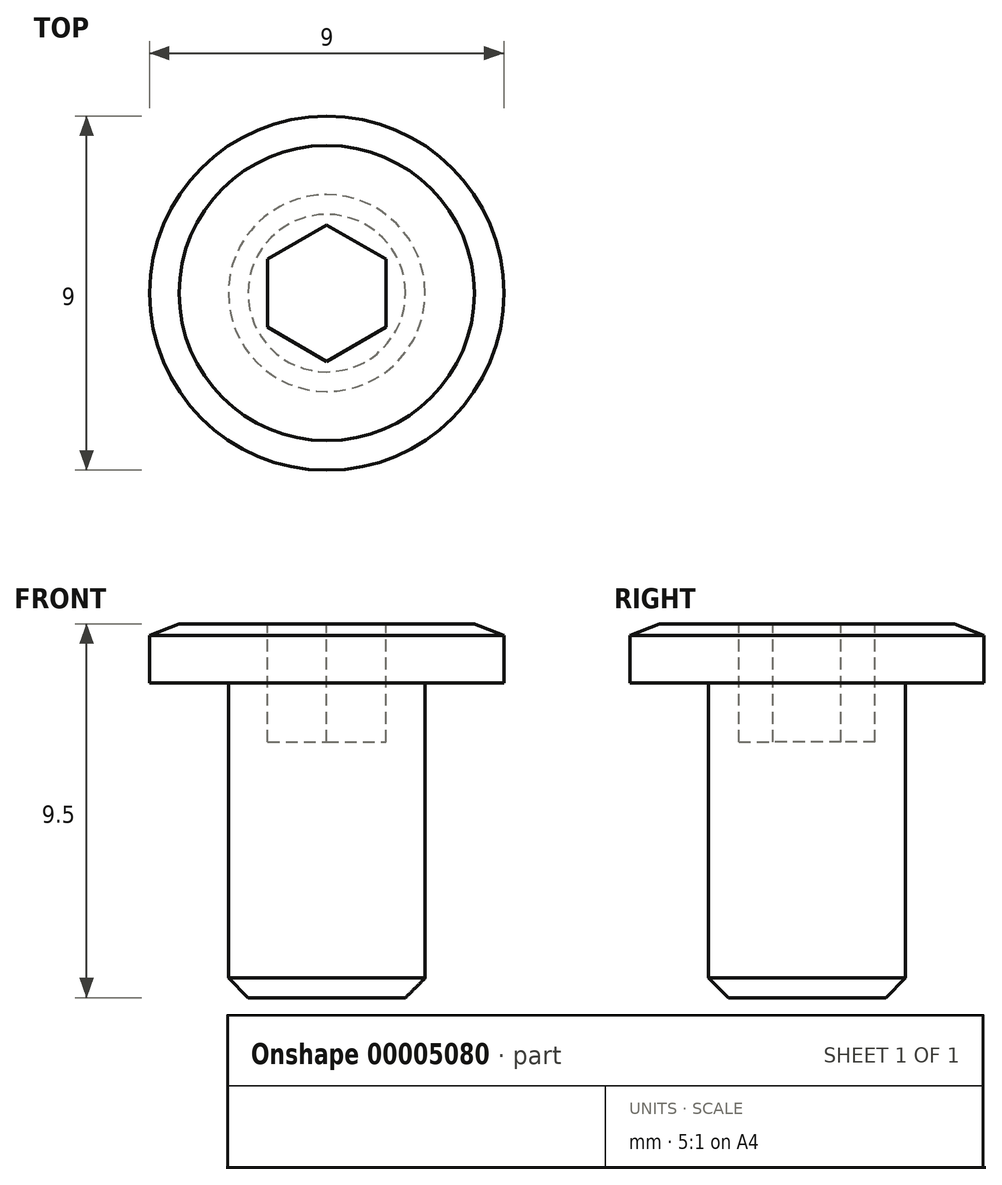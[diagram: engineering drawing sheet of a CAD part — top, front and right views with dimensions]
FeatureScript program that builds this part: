
annotation { "Feature Type Name" : "Feature", "Feature Type Description" : "" }
export const myFeature = defineFeature(function(context is Context, id is Id, definition is map)
    precondition{}
    {
        {
            var Q0;
            Q0=qCreatedBy(makeId("Front.planeOp"),FACE);
            var sketch = newSketch(context, id + "F0", { "sketchPlane" : qUnion([Q0])});
            skLineSegment(sketch, "E0", {"start": v(0, 0) * mm, "end": v(2.5, 0) * mm});
            skLineSegment(sketch, "E1", {"start": v(2.5, 0) * mm, "end": v(2.5, 8) * mm});
            skLineSegment(sketch, "E2", {"start": v(2.5, 8) * mm, "end": v(4.5, 8) * mm});
            skLineSegment(sketch, "E3", {"start": v(4.5, 8) * mm, "end": v(4.5, 9.2) * mm});
            skLineSegment(sketch, "E4", {"start": v(0, 9.5) * mm, "end": v(0, 0) * mm});
            skLineSegment(sketch, "E5", {"start": v(0, 9.5) * mm, "end": v(3.75, 9.5) * mm});
            skLineSegment(sketch, "E6", {"start": v(3.75, 9.5) * mm, "end": v(4.5, 9.2) * mm});
            skSolve(sketch);
        }
        {
            var Q0;
            Q0=makeQuery(id+"F0.imprint","IMPRINT",FACE,{"disambiguationData":[TD([[makeQuery(id+"F0.imprint","IMPRINT",EDGE,{"derivedFrom":sQuery(id+"F0.wireOp",EDGE,"E0")}),1.0]])]});
            var Q1;
            Q1=sQuery(id+"F0.wireOp",EDGE,"E4");
            revolve(context, id + "F1", {"entities" : qUnion([Q0]), "axis" : qUnion([Q1]), "revolveType" : RevolveType.FULL});
        }
        {
            var Q0;
            Q0=makeQuery(id+"F1.opRevolve","SWEPT_EDGE",EDGE,{"disambiguationData":[OSD([sQuery(id+"F0.wireOp",EDGE,"E0"),sQuery(id+"F0.wireOp",EDGE,"E1")])]});
            chamfer(context, id + "F2", {"entities" : qUnion([Q0]), "width" : 0.5 * mm, "tangentPropagation" : true});
        }
        {
            var Q0;
            Q0=makeQuery(id+"F1.opRevolve","SWEPT_FACE",FACE,{"disambiguationData":[OSD([sQuery(id+"F0.wireOp",EDGE,"E5")])]});
            var sketch = newSketch(context, id + "F3", { "sketchPlane" : qUnion([Q0])});
            skCircle(sketch, "E7.cCircle", {"center": v(0, 0) * mm, "radius": 1.5 * mm, "construction": true});
            skLineSegment(sketch, "E7.0", {"start": v(1.5, 0.87) * mm, "end": v(1.5, -0.87) * mm});
            skLineSegment(sketch, "E7.1", {"start": v(1.5, -0.87) * mm, "end": v(0, -1.73) * mm});
            skLineSegment(sketch, "E7.2", {"start": v(0, -1.73) * mm, "end": v(-1.5, -0.87) * mm});
            skLineSegment(sketch, "E7.3", {"start": v(-1.5, -0.87) * mm, "end": v(-1.5, 0.87) * mm});
            skLineSegment(sketch, "E7.4", {"start": v(-1.5, 0.87) * mm, "end": v(0, 1.73) * mm});
            skLineSegment(sketch, "E7.5", {"start": v(0, 1.73) * mm, "end": v(1.5, 0.87) * mm});
            skPoint(sketch, "E7.0.midPoint", {"position": v(1.5, 0) * mm});
            skSolve(sketch);
        }
        {
            var Q0;
            Q0=makeQuery(id+"F3.imprint","IMPRINT",FACE,{"disambiguationData":[TD([[makeQuery(id+"F3.imprint","IMPRINT",EDGE,{"derivedFrom":sQuery(id+"F3.wireOp",EDGE,"E7.0")}),-1.0]])]});
            extrude(context, id + "F4", {"entities" : qUnion([Q0]), "operationType" : NewBodyOperationType.REMOVE, "oppositeDirection" : true, "depth" : 3 * mm});
        }
    });
